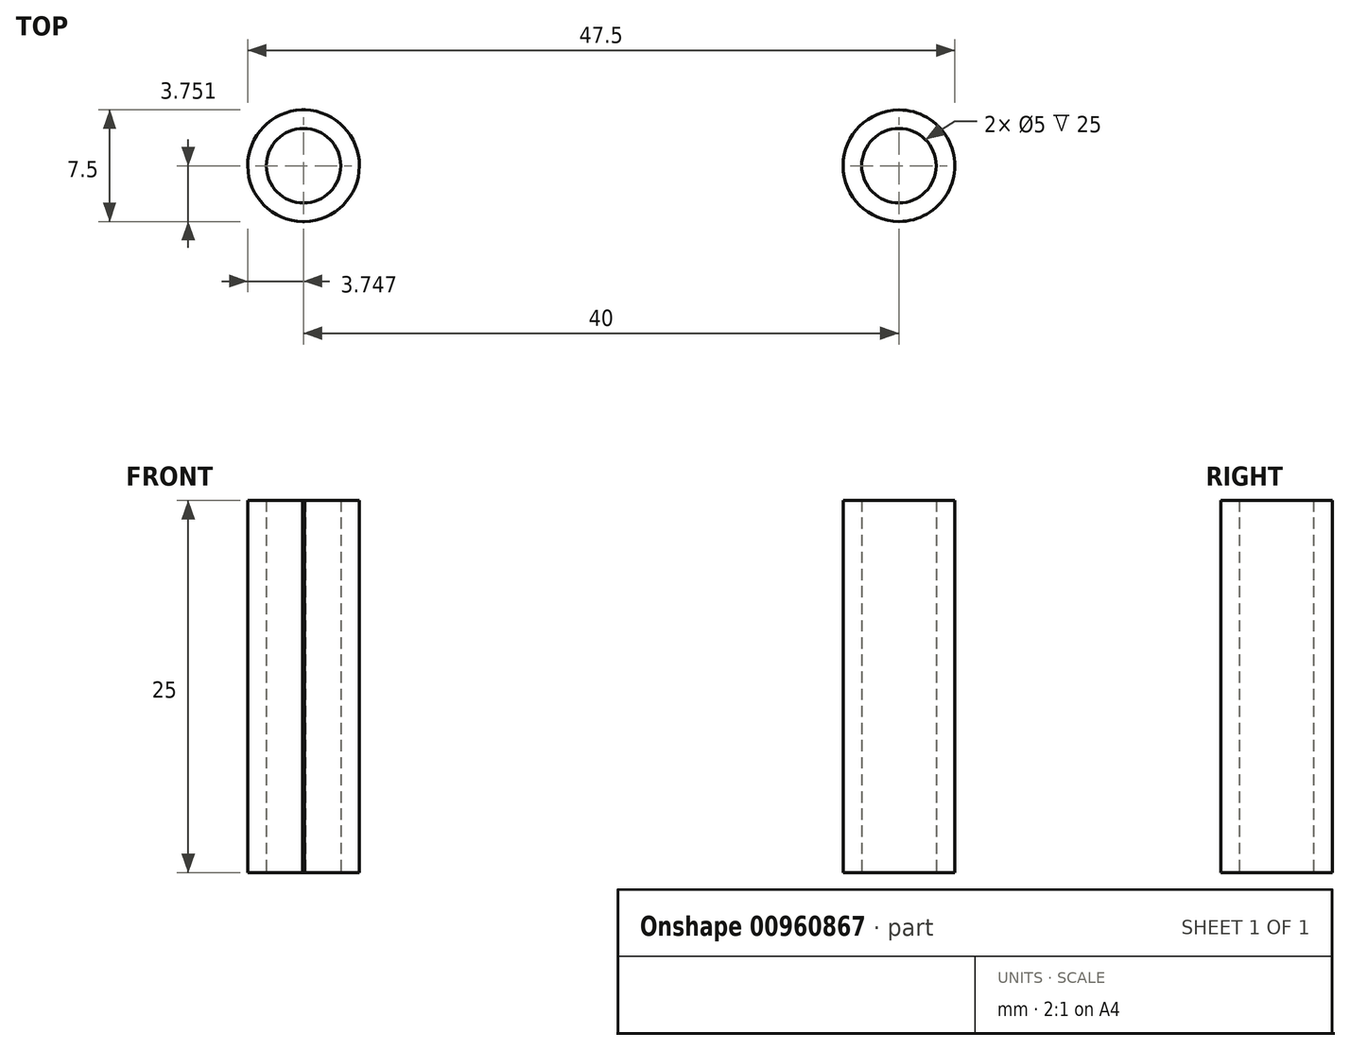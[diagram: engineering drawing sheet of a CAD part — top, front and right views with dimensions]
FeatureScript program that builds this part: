
annotation { "Feature Type Name" : "Feature", "Feature Type Description" : "" }
export const myFeature = defineFeature(function(context is Context, id is Id, definition is map)
    precondition{}
    {
        {
            var Q0;
            Q0=qCreatedBy(makeId("Top.planeOp"),FACE);
            var sketch = newSketch(context, id + "F0", { "sketchPlane" : qUnion([Q0])});
            skCircle(sketch, "E0", {"center": v(-22.41, 0.16) * mm, "radius": 2.5 * mm});
            skCircle(sketch, "E1", {"center": v(17.59, 0.16) * mm, "radius": 2.5 * mm});
            skCircle(sketch, "E2", {"center": v(-22.41, 0.16) * mm, "radius": 3.75 * mm});
            skCircle(sketch, "E3", {"center": v(17.59, 0.16) * mm, "radius": 3.75 * mm});
            skLineSegment(sketch, "E4", {"start": v(-22.53, 3.9) * mm, "end": v(17.59, 3.91) * mm});
            skLineSegment(sketch, "E5", {"start": v(-22.48, -3.59) * mm, "end": v(17.59, -3.59) * mm});
            skSolve(sketch);
        }
        {
            var Q0;
            {var subQ0=sQuery(id+"F0.wireOp",EDGE,"E4");var subQ1=sQuery(id+"F0.wireOp",EDGE,"E2");var subQ2=makeQuery(id+"F0.imprint","INTERSECT",VERTEX,{"disambiguationData":[OD(0.0)],"derivedFrom":[subQ1,subQ0]});Q0=makeQuery(id+"F0.imprint","IMPRINT",FACE,{"disambiguationData":[TD([[makeQuery(id+"F0.imprint","IMPRINT",EDGE,{"disambiguationData":[TD([[subQ2,1.0]])],"derivedFrom":subQ1}),1.0]])]});}
            var Q1;
            {var subQ0=sQuery(id+"F0.wireOp",EDGE,"E5");var subQ1=sQuery(id+"F0.wireOp",EDGE,"E2");var subQ2=makeQuery(id+"F0.imprint","INTERSECT",VERTEX,{"disambiguationData":[OD(0.0)],"derivedFrom":[subQ1,subQ0]});Q1=makeQuery(id+"F0.imprint","IMPRINT",FACE,{"disambiguationData":[TD([[makeQuery(id+"F0.imprint","IMPRINT",EDGE,{"disambiguationData":[TD([[subQ2,-1.0]])],"derivedFrom":subQ1}),1.0]])]});}
            var Q2;
            Q2=makeQuery(id+"F0.imprint","IMPRINT",FACE,{"disambiguationData":[TD([[makeQuery(id+"F0.imprint","IMPRINT",EDGE,{"derivedFrom":sQuery(id+"F0.wireOp",EDGE,"E1")}),-1.0]])]});
            var Q3;
            Q3=makeQuery(id+"F0.imprint","IMPRINT",FACE,{"disambiguationData":[TD([[makeQuery(id+"F0.imprint","IMPRINT",EDGE,{"derivedFrom":sQuery(id+"F0.wireOp",EDGE,"E0")}),-1.0]])]});
            var Q4;
            {var subQ0=sQuery(id+"F0.wireOp",EDGE,"E4");var subQ1=sQuery(id+"F0.wireOp",EDGE,"E2");var subQ2=makeQuery(id+"F0.imprint","INTERSECT",VERTEX,{"disambiguationData":[OD(1.0)],"derivedFrom":[subQ1,subQ0]});Q4=makeQuery(id+"F0.imprint","IMPRINT",FACE,{"disambiguationData":[TD([[makeQuery(id+"F0.imprint","IMPRINT",EDGE,{"disambiguationData":[TD([[subQ2,1.0]])],"derivedFrom":subQ1}),-1.0]])]});}
            extrude(context, id + "F1", {"entities" : qUnion([Q0, Q1, Q2, Q3, Q4]), "depth" : 25 * mm, "offsetDistance" : 25 * mm});
        }
        {
            var Q0;
            Q0=makeQuery(id+"F1.opExtrude","SWEPT_FACE",FACE,{"disambiguationData":[OSD([sQuery(id+"F0.wireOp",EDGE,"E5")])]});
            var sketch = newSketch(context, id + "F2", { "sketchPlane" : qUnion([Q0])});
            skCircle(sketch, "E6", {"center": v(-2.41, 15) * mm, "radius": 2.5 * mm});
            skCircle(sketch, "E7", {"center": v(5.59, 15) * mm, "radius": 1.75 * mm});
            skCircle(sketch, "E8", {"center": v(-10.41, 15) * mm, "radius": 1.75 * mm});
            skSolve(sketch);
        }
        {
            var Q0;
            Q0=makeQuery(id+"F2.imprint","IMPRINT",FACE,{"disambiguationData":[TD([[makeQuery(id+"F2.imprint","IMPRINT",EDGE,{"derivedFrom":sQuery(id+"F2.wireOp",EDGE,"E6")}),1.0]])]});
            var Q1;
            Q1=makeQuery(id+"F2.imprint","IMPRINT",FACE,{"disambiguationData":[TD([[makeQuery(id+"F2.imprint","IMPRINT",EDGE,{"derivedFrom":sQuery(id+"F2.wireOp",EDGE,"E8")}),1.0]])]});
            var Q2;
            Q2=makeQuery(id+"F2.imprint","IMPRINT",FACE,{"disambiguationData":[TD([[makeQuery(id+"F2.imprint","IMPRINT",EDGE,{"derivedFrom":sQuery(id+"F2.wireOp",EDGE,"E7")}),1.0]])]});
            extrude(context, id + "F3", {"entities" : qUnion([Q0, Q1, Q2]), "operationType" : NewBodyOperationType.REMOVE, "oppositeDirection" : true, "depth" : 25 * mm, "offsetDistance" : 25 * mm});
        }
    });
